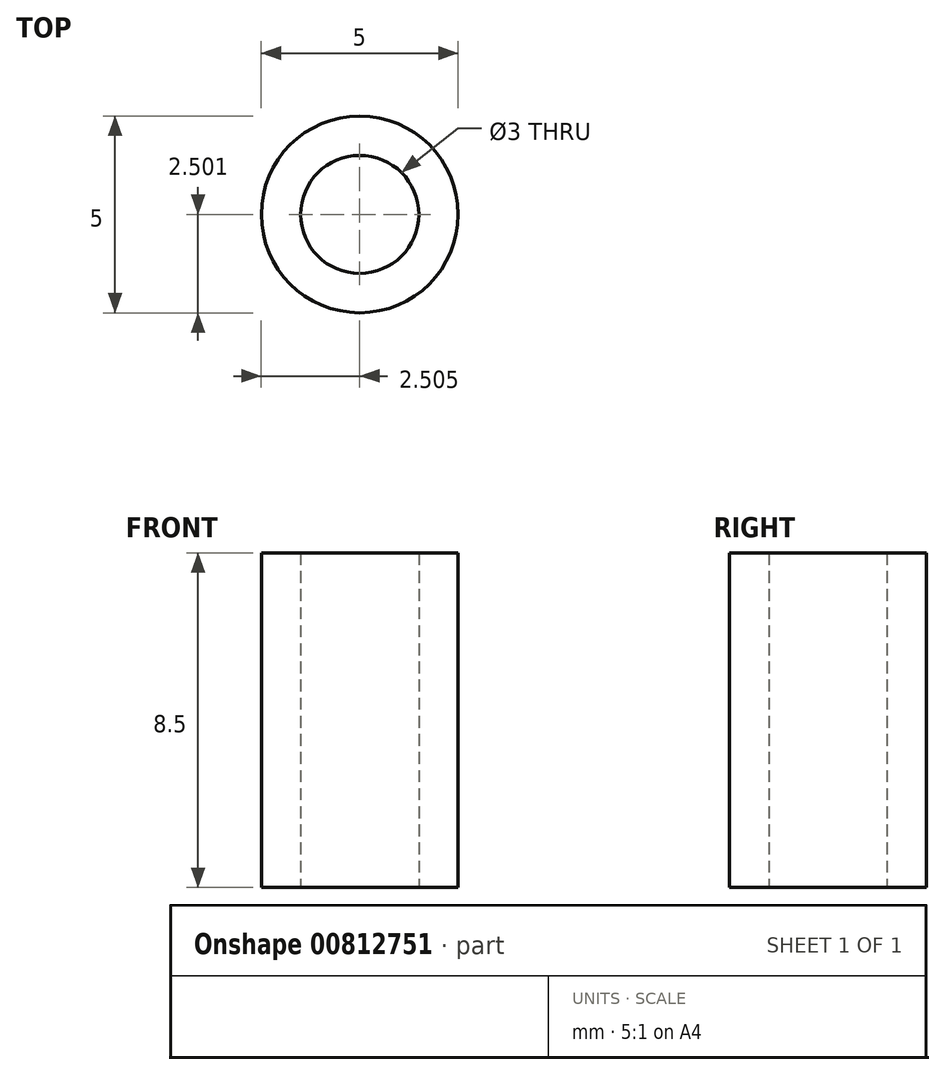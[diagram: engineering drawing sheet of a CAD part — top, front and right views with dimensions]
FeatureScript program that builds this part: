
annotation { "Feature Type Name" : "Feature", "Feature Type Description" : "" }
export const myFeature = defineFeature(function(context is Context, id is Id, definition is map)
    precondition{}
    {
        {
            var Q0;
            Q0=qCreatedBy(makeId("Top.planeOp"),FACE);
            var sketch = newSketch(context, id + "F0", { "sketchPlane" : qUnion([Q0])});
            skCircle(sketch, "E0", {"center": v(-40.72, 53.35) * mm, "radius": 1.5 * mm});
            skCircle(sketch, "E1", {"center": v(-40.72, 53.35) * mm, "radius": 2.5 * mm});
            skSolve(sketch);
        }
        {
            var Q0;
            Q0=makeQuery(id+"F0.imprint","IMPRINT",FACE,{"disambiguationData":[TD([[makeQuery(id+"F0.imprint","IMPRINT",EDGE,{"derivedFrom":sQuery(id+"F0.wireOp",EDGE,"E0")}),-1.0]])]});
            extrude(context, id + "F1", {"entities" : qUnion([Q0]), "depth" : 8.5 * mm, "offsetDistance" : 25 * mm});
        }
    });
